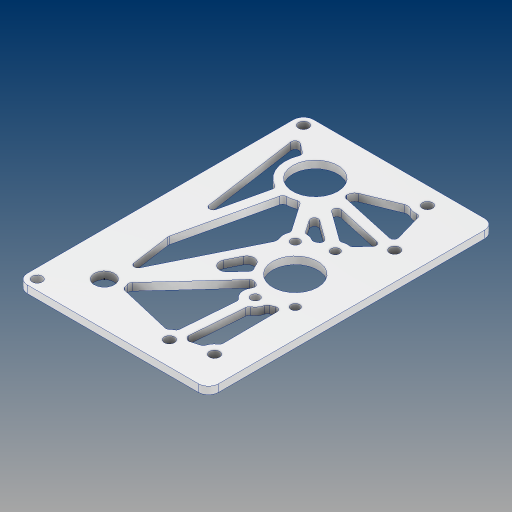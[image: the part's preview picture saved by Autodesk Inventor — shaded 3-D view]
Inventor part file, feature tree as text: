
AUTODESK INVENTOR PART (.ipt)
format: ipt  version: 2024.3 (Build 283343000, 343)  size: 631,808 bytes
history: native  units: in
note: dims shown in document units (in); Inventor stores cm internally (conversion verified against a paired STEP export)
features: sketch x3, extrude x3, projected_geometry x1
ambient origin geometry x8: Origin, YZ Plane, XZ Plane, XY Plane, X Axis, Y Axis, Z Axis, Center Point
bodies: Body1 (feature_tree)
feature tree (7):
  sketch  "Sketch1"  dims[d1=1.125in d2=0.5in]
  extrude  "Extrusion2"  Depth=0.5in
  extrude  "Extrusion5"  Depth=0.5in
  extrude  "Extrusion6"  Depth=0.1875in
  sketch  "Sketch7"  dims[d6=0.256in d7=0.256in d8=0.5in d9=0.5in d17=2.44in d18=2.44in d19=2.0in d20=0.22in d21=3.1496in d23=360.0deg d25=1.125in d26=1.8in d27=1.8in d31=0.188in d32=0.256in d33=0.5in d34=0.256in d35=0.5in d38=0.1875in d39=0.1875in d40=0.1875in d41=0.25in d42=0.25in d43=0.1875in d44=0.0in d134=0.256in d135=0.256in d136=0.5in d162=0.457in d163=3.3875in d165=6.7749in d166=0.6043in d167=4.5in d168=1.0in d169=0.0in d199=0.188in d200=0.1875in d201=0.1875in d202=0.1875in d203=0.1875in d204=0.188in d205=0.188in d206=0.188in d207=0.188in d208=0.188in d209=0.125in d210=0.125in d211=0.093in d212=0.093in d213=0.093in d217=0.125in d218=0.125in d219=0.125in d220=0.125in d223=0.125in d224=0.125in d225=0.125in d227=0.093in d228=0.093in d229=0.093in d230=0.125in d231=0.125in d233=0.093in d234=0.093in d235=0.093in d236=0.125in d237=0.125in d238=0.125in d239=0.125in d240=0.093in d241=0.125in d243=0.125in d244=0.125in d245=0.093in d246=0.093in d247=0.125in d248=0.125in d249=0.125in d250=0.125in d251=0.093in d252=0.093in d253=0.093in d254=0.125in d256=0.125in d257=0.093in d258=0.093in d259=0.093in d260=0.093in d261=0.125in d262=0.1875in d263=0.125in d264=0.125in d265=0.125in d266=0.188in d267=0.093in d268=0.093in d269=0.125in d270=0.125in d271=0.125in d273=0.188in d274=0.093in d275=0.125in d276=0.188in d277=0.093in d278=0.093in d279=0.125in d280=0.125in d281=0.125in d282=0.093in d283=0.125in d284=0.125in d285=0.125in d286=0.093in d287=1.0in d288=0.0in d289=1.568in d290=1.568in d293=0.125in d294=0.125in d295=0.125in d298=0.093in d299=0.093in d300=0.1875in d301=0.1875in d302=0.1875in d303=0.093in d304=0.1875in d305=0.125in d306=0.1875in]
  sketch  "Sketch6"  dims[d4=0.5in d5=0.5in]
  projected_geometry  "Projected Loop3"
